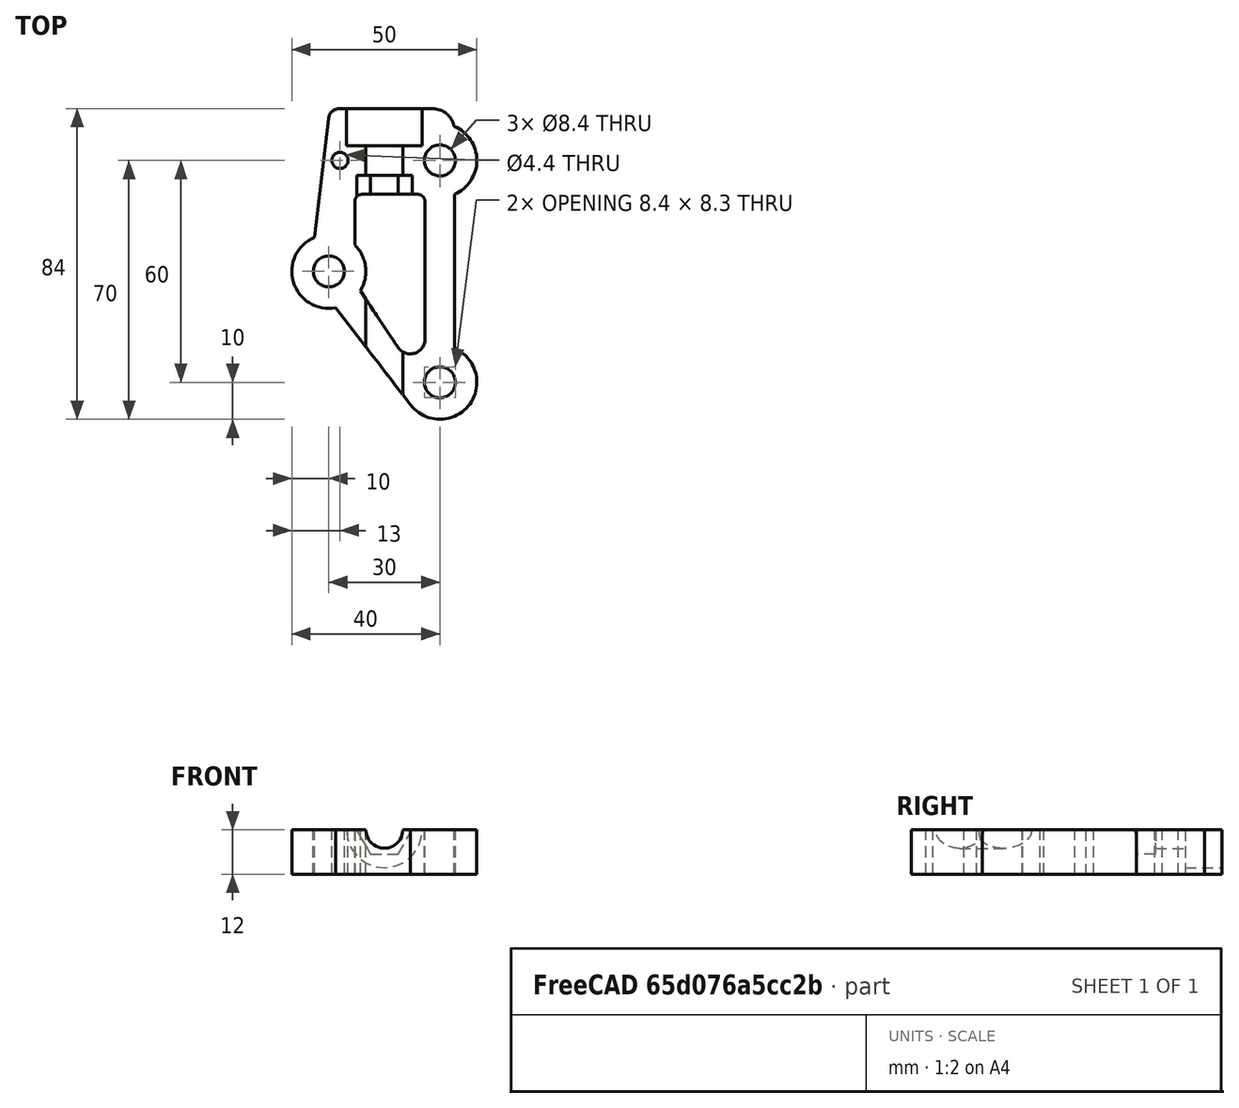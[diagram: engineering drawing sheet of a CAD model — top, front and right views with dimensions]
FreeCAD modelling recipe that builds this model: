
FCSTD DOCUMENT  (FreeCAD 0.15R4664 (Git))
Label: y_nut_holder_A
License: All rights reserved
LicenseURL: http://en.wikipedia.org/wiki/All_rights_reserved
objects: Part::Cylinder×9, Part::Cut×6, Part::Fillet×4, Part::Feature×3, Part::MultiFuse×3, Part::Chamfer×2, Part::Box×1, Part::Prism×1
note: 29 computed .brp shape members not serialized (recipe doc carries the construction recipe); baked Part::Feature solids carry a one-line shape summary decoded from their .brp

FEATURE [Part::Box] Box  label="Cubo"
  Height = 12
  Length = 39
  Placement = pos=(5,14,0) rot=(0,0,1;0rad)
  Width = 80
FEATURE [Part::Cylinder] Cylinder  label="Cilindro"
  Angle = 360
  Height = 12
  Placement = pos=(40,20,0) rot=(0,0,1;0rad)
  Radius = 10
FEATURE [Part::Cylinder] Cylinder001  label="Cilindro001"
  Angle = 360
  Height = 12
  Placement = pos=(10,50,0) rot=(0,0,1;0rad)
  Radius = 10
FEATURE [Part::Cylinder] Cylinder002  label="Cilindro002"
  Angle = 360
  Height = 12
  Placement = pos=(40,80,0) rot=(0,0,1;0rad)
  Radius = 10
FEATURE [Part::Cylinder] Cylinder007  label="screw_hole_2"
  Angle = 360
  Height = 14
  Placement = pos=(13,80,-1) rot=(0,0,1;0rad)
  Radius = 2.2
FEATURE [Part::Feature] YnutholderL001001  label="YnutholderL002"
  Placement = pos=(50,10,0) rot=(0,0,1;1.5708rad)
  shape: bbox 50 x 84 x 12 mm, 1642 faces, 0 solids (baked)
FEATURE [Part::MultiFuse] Fusion
  Shapes = -> [Cylinder001,Cylinder,Cylinder002]
FEATURE [Part::Chamfer] Chamfer
  Base = -> Box
  Edges = 1 edges: [Edge1 r1=35 r2=27]
FEATURE [Part::Chamfer] Chamfer001
  Base = -> Chamfer
  Edges = 1 edges: [Edge3 r1=44.9 r2=5.2]
FEATURE [Part::Fillet] Fillet
  Base = -> Chamfer001
  Edges = 1 edges r=3: [Edge11]
FEATURE [Part::Fillet] Fillet001
  Base = -> Fillet
  Edges = 1 edges r=6: [Edge16]
FEATURE [Part::Cylinder] Cylinder009  label="Cilindro003"
  Angle = 360
  Height = 14
  Placement = pos=(40,20,-1) rot=(0,0,1;0rad)
  Radius = 4.2
FEATURE [Part::Cylinder] Cylinder010  label="Cilindro004"
  Angle = 360
  Height = 14
  Placement = pos=(40,80,-1) rot=(0,0,1;0rad)
  Radius = 4.2
FEATURE [Part::Cylinder] Cylinder011  label="Cilindro005"
  Angle = 360
  Height = 14
  Placement = pos=(10,50,-1) rot=(0,0,1;0rad)
  Radius = 4.2
FEATURE [Part::MultiFuse] Fusion004
  Shapes = -> [Cylinder009,Cylinder010,Cylinder011]
FEATURE [Part::Feature] Pad001
  Placement = pos=(50,10,-1) rot=(0,0,1;1.5708rad)
  shape: bbox 19 x 52.4 x 14 mm, 6 faces (baked)
FEATURE [Part::Cut] Cut
  Base = -> Fillet001
  Tool = -> Pad001
FEATURE [Part::Fillet] Fillet002
  Base = -> Cut
  Edges = 2 edges r=2: [Edge31,Edge33]
FEATURE [Part::Fillet] Fillet003
  Base = -> Fillet002
  Edges = 1 edges r=4: [Edge17]
FEATURE [Part::MultiFuse] Fusion005
  Shapes = -> [Fillet003,Fusion]
FEATURE [Part::Cut] Cut001
  Base = -> Fusion005
  Tool = -> Fusion004
FEATURE [Part::Cylinder] Cylinder012  label="Cilindro006"
  Angle = 360
  Height = 80
  Placement = pos=(25,15,12) rot=(-1,0,0;1.5708rad)
  Radius = 5
FEATURE [Part::Cut] Cut002
  Base = -> Cut001
  Tool = -> Cylinder012
FEATURE [Part::Prism] Prism001  label="Prisma001"
  Circumradius = 7.5
  Height = 7
  Placement = pos=(25,76,12) rot=(1,0,0;1.5708rad)
  Polygon = 6
FEATURE [Part::Cut] Cut003
  Base = -> Cut002
  Tool = -> Prism001
FEATURE [Part::Cylinder] Cylinder013  label="Cilindro007"
  Angle = 360
  Height = 11
  Placement = pos=(25,84,12) rot=(-1,0,0;1.5708rad)
  Radius = 10.2
FEATURE [Part::Cut] Cut004
  Base = -> Cut003
  Tool = -> Cylinder013
FEATURE [Part::Cut] Cut005
  Base = -> Cut004
  Tool = -> Cylinder007
FEATURE [Part::Feature] Cut005_solid  label="Cut005 (Solid)"
  shape: bbox 50 x 84 x 12 mm, 32 faces (baked)
